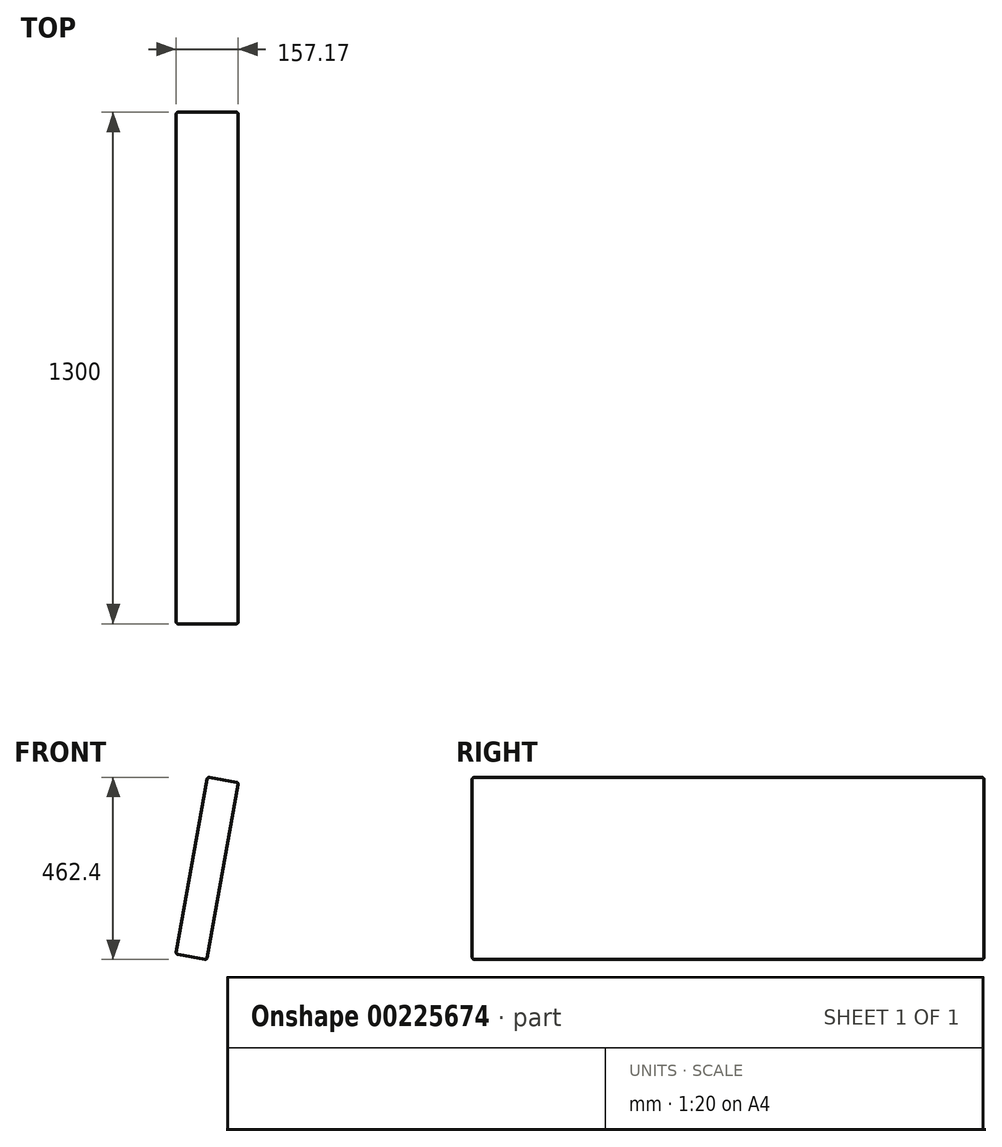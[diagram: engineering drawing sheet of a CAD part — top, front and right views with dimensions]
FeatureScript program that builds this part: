
annotation { "Feature Type Name" : "Feature", "Feature Type Description" : "" }
export const myFeature = defineFeature(function(context is Context, id is Id, definition is map)
    precondition{}
    {
        {
            var Q0;
            Q0=qCreatedBy(makeId("Front.planeOp"),FACE);
            var sketch = newSketch(context, id + "F0", { "sketchPlane" : qUnion([Q0])});
            skLineSegment(sketch, "E0.bottom", {"start": v(-40, 225) * mm, "end": v(40, 225) * mm, "construction": true});
            skLineSegment(sketch, "E0.top", {"start": v(-40, -225) * mm, "end": v(40, -225) * mm, "construction": true});
            skLineSegment(sketch, "E0.left", {"start": v(-40, 225) * mm, "end": v(-40, -225) * mm, "construction": true});
            skLineSegment(sketch, "E0.right", {"start": v(40, 225) * mm, "end": v(40, -225) * mm, "construction": true});
            skLineSegment(sketch, "E1", {"start": v(0, 225) * mm, "end": v(0, -225) * mm, "construction": true});
            skLineSegment(sketch, "E2", {"start": v(-40, 0) * mm, "end": v(40, 0) * mm, "construction": true});
            skLineSegment(sketch, "E3", {"start": v(40, 225) * mm, "end": v(-40, -225) * mm});
            skLineSegment(sketch, "E4", {"start": v(40, 225) * mm, "end": v(-38.77, 239) * mm});
            skLineSegment(sketch, "E5", {"start": v(-40, -225) * mm, "end": v(-118.77, -211) * mm});
            skLineSegment(sketch, "E6", {"start": v(-38.77, 239) * mm, "end": v(-118.77, -211) * mm});
            skSolve(sketch);
        }
        {
            var Q0;
            Q0=makeQuery(id+"F0.imprint","IMPRINT",FACE,{"disambiguationData":[TD([[makeQuery(id+"F0.imprint","IMPRINT",EDGE,{"derivedFrom":sQuery(id+"F0.wireOp",EDGE,"E3")}),-1.0]])]});
            extrude(context, id + "F1", {"entities" : qUnion([Q0]), "endBound" : BoundingType.SYMMETRIC, "depth" : 1300 * mm});
        }
        {
            var Q0;
            Q0=makeQuery(id+"F1.opExtrude","SWEPT_EDGE",EDGE,{"disambiguationData":[OSD([sQuery(id+"F0.wireOp",EDGE,"E3"),sQuery(id+"F0.wireOp",EDGE,"E4")])]});
            var Q1;
            Q1=makeQuery(id+"F1.opExtrude","SWEPT_EDGE",EDGE,{"disambiguationData":[OSD([sQuery(id+"F0.wireOp",EDGE,"E4"),sQuery(id+"F0.wireOp",EDGE,"E6")])]});
            var Q2;
            Q2=makeQuery(id+"F1.opExtrude","CAP_EDGE",EDGE,{"disambiguationData":[OSD([sQuery(id+"F0.wireOp",EDGE,"E4")])],"isStart":false});
            var Q3;
            Q3=makeQuery(id+"F1.opExtrude","CAP_EDGE",EDGE,{"disambiguationData":[OSD([sQuery(id+"F0.wireOp",EDGE,"E3")])],"isStart":false});
            var Q4;
            Q4=makeQuery(id+"F1.opExtrude","CAP_EDGE",EDGE,{"disambiguationData":[OSD([sQuery(id+"F0.wireOp",EDGE,"E6")])],"isStart":false});
            var Q5;
            Q5=makeQuery(id+"F1.opExtrude","CAP_EDGE",EDGE,{"disambiguationData":[OSD([sQuery(id+"F0.wireOp",EDGE,"E5")])],"isStart":false});
            var Q6;
            Q6=makeQuery(id+"F1.opExtrude","SWEPT_EDGE",EDGE,{"disambiguationData":[OSD([sQuery(id+"F0.wireOp",EDGE,"E3"),sQuery(id+"F0.wireOp",EDGE,"E5")])]});
            var Q7;
            Q7=makeQuery(id+"F1.opExtrude","SWEPT_EDGE",EDGE,{"disambiguationData":[OSD([sQuery(id+"F0.wireOp",EDGE,"E5"),sQuery(id+"F0.wireOp",EDGE,"E6")])]});
            var Q8;
            Q8=makeQuery(id+"F1.opExtrude","CAP_FACE",FACE,{"disambiguationData":[OSD([sQuery(id+"F0.wireOp",EDGE,"E3"),sQuery(id+"F0.wireOp",EDGE,"E4"),sQuery(id+"F0.wireOp",EDGE,"E5"),sQuery(id+"F0.wireOp",EDGE,"E6")])],"isStart":true});
            var Q9;
            Q9=makeQuery(id+"F1.opExtrude","CAP_EDGE",EDGE,{"disambiguationData":[OSD([sQuery(id+"F0.wireOp",EDGE,"E3")])],"isStart":true});
            fillet(context, id + "F2", {"entities" : qUnion([Q0, Q1, Q2, Q3, Q4, Q5, Q6, Q7, Q8, Q9]), "radius" : 5 * mm, "tangentPropagation" : true, "allowEdgeOverflow" : false});
        }
    });
